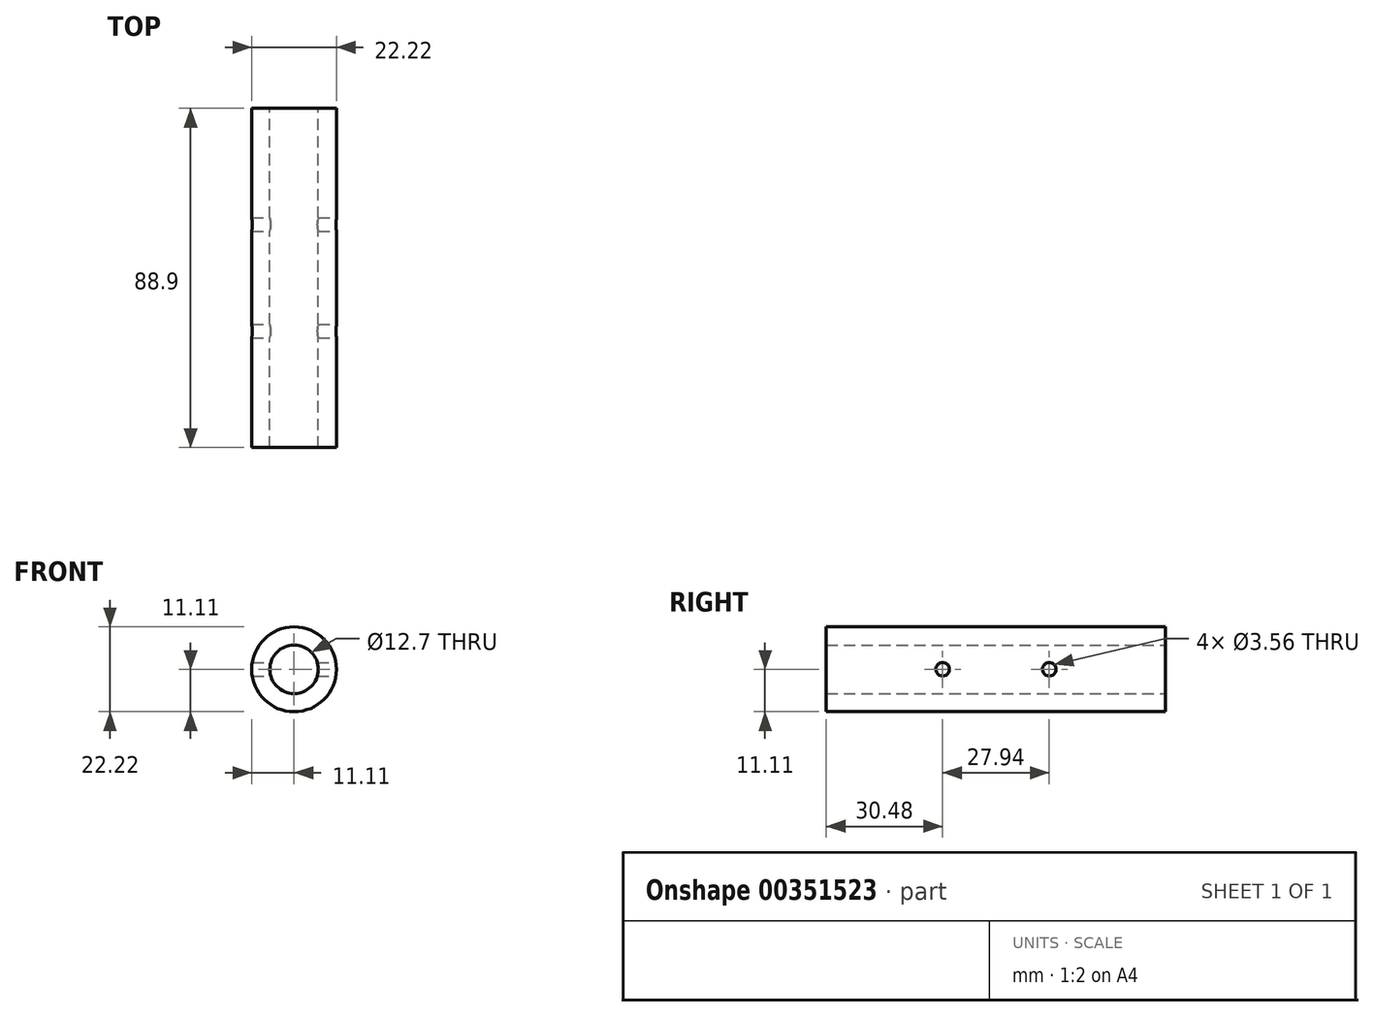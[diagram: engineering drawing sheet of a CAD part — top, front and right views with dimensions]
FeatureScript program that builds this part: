
annotation { "Feature Type Name" : "Feature", "Feature Type Description" : "" }
export const myFeature = defineFeature(function(context is Context, id is Id, definition is map)
    precondition{}
    {
        {
            var Q0;
            Q0=qCreatedBy(makeId("Front.planeOp"),FACE);
            var sketch = newSketch(context, id + "F0", { "sketchPlane" : qUnion([Q0])});
            skCircle(sketch, "E0", {"center": v(0, 0) * mm, "radius": 11.11 * mm});
            skCircle(sketch, "E1", {"center": v(0, 0) * mm, "radius": 6.35 * mm});
            skSolve(sketch);
        }
        {
            var Q0;
            Q0 = qSketchRegion(id + "F0", true);
            extrude(context, id + "F1", {"entities" : qUnion([Q0]), "depth" : 88.9 * mm, "symmetric" : true});
        }
        {
            var Q0;
            Q0=qCreatedBy(makeId("Right.planeOp"),FACE);
            var sketch = newSketch(context, id + "F2", { "sketchPlane" : qUnion([Q0])});
            skCircle(sketch, "E2", {"center": v(13.97, 0) * mm, "radius": 1.78 * mm});
            skCircle(sketch, "E3", {"center": v(-13.97, 0) * mm, "radius": 1.78 * mm});
            skSolve(sketch);
        }
        {
            var Q0;
            Q0 = qSketchRegion(id + "F2", true);
            extrude(context, id + "F3", {"entities" : qUnion([Q0]), "operationType" : NewBodyOperationType.REMOVE, "endBound" : BoundingType.THROUGH_ALL, "oppositeDirection" : true, "depth" : 25.4 * mm, "hasSecondDirection" : true, "secondDirectionBound" : BoundingType.THROUGH_ALL, "secondDirectionOppositeDirection" : false, "secondDirectionDepth" : 25.4 * mm});
        }
    });
